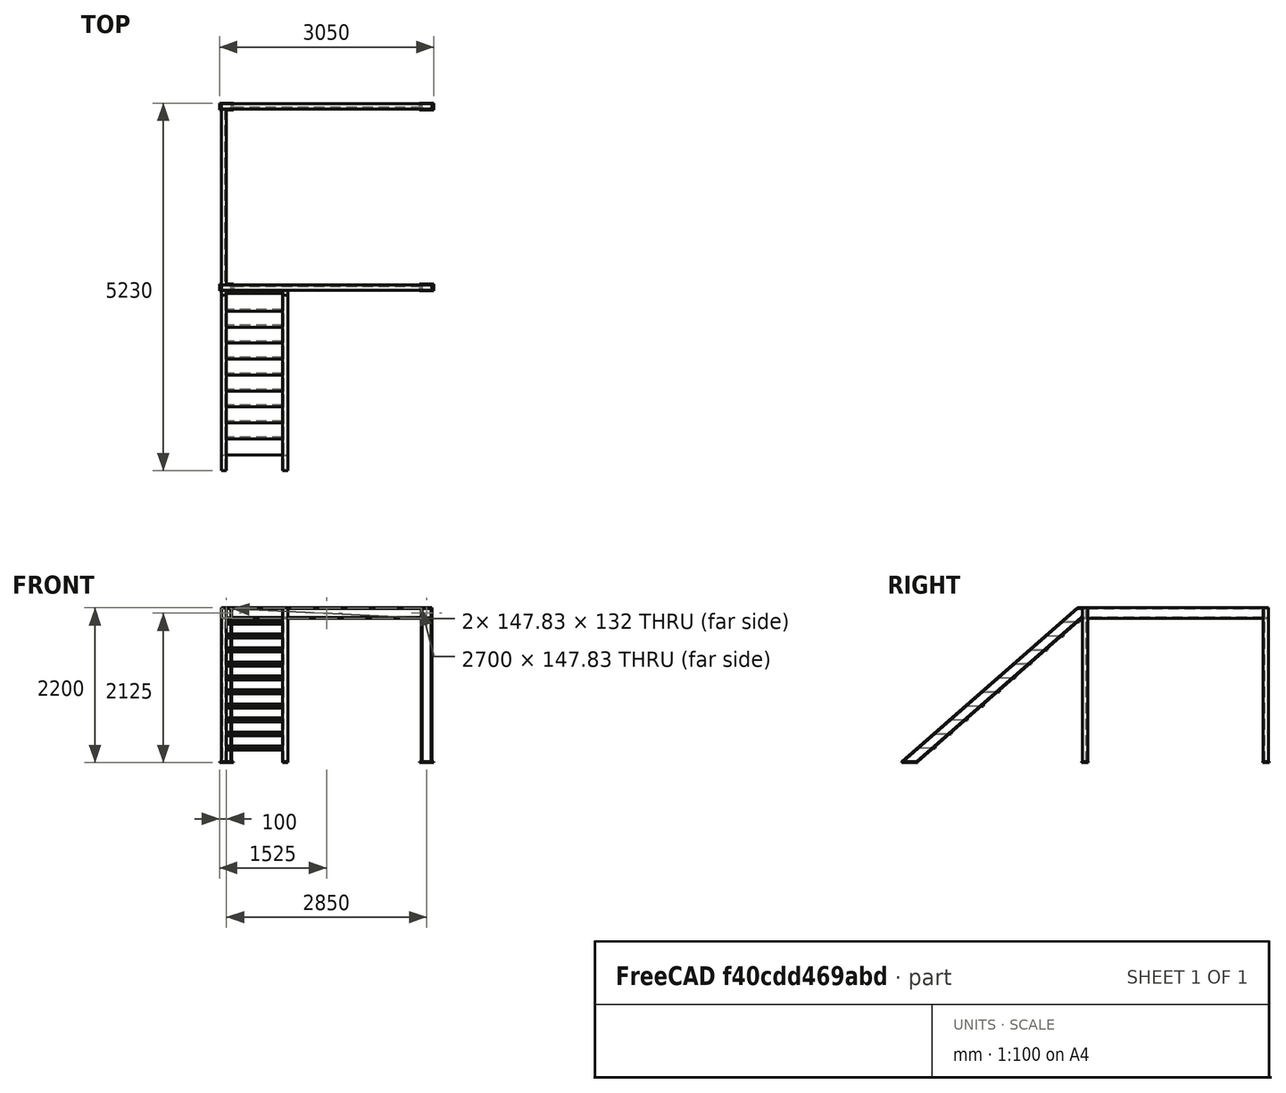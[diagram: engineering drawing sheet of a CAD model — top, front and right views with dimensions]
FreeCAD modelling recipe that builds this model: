
FCSTD DOCUMENT  (FreeCAD 0.21R30492 (Git))
Label: test2
License: All rights reserved
LicenseURL: http://en.wikipedia.org/wiki/All_rights_reserved
objects: App::FeaturePython×20, Part::FeaturePython×4, Part::Mirroring×2
note: 6 computed .brp shape members not serialized (recipe doc carries the construction recipe); baked Part::Feature solids carry a one-line shape summary decoded from their .brp

FEATURE [Part::FeaturePython] s06C150x75x9  # WARN: FeaturePython — macro-defined, semantics opaque (R4)
  B = 95
  BasePlate = true
  H = 2200
  L1 = 3000
  W = 200
  key = 5
  key1 = 1
  size = 3
  t0 = 6
FEATURE [Part::FeaturePython] C150x75x9  # WARN: FeaturePython — macro-defined, semantics opaque (R4)
  L = 2500
  Placement = pos=(2962.5,-2.62e-14,2125) rot=(1,0,0;1.5708rad)
  Solid = true
  size = 4
  standard = SS
FEATURE [Part::FeaturePython] s06C150x75x9_001  # a2plus imported part (geometry in sourceFile) (typed FeaturePython)
  a2p_Version = 0.4.60i
  fixedPosition = true
  localSourceObject = s06C150x75x9
  objectType = a2pPart
  sourceFile = converted
  subassemblyImport = false
  timeLastImport = 1.6781e+09
  updateColors = true
FEATURE [App::FeaturePython] pointIdentity_001  label="pointIdentity_001__s06C150x75x9_001"  # a2plus constraint (typed FeaturePython)
  Object1 = C150x75x9
  Object2 = s06C150x75x9_001
  ParentTreeObject = -> C150x75x9
  SubElement1 = Vertex23
  SubElement2 = Vertex22
  Suppressed = false
  Type = pointIdentity
FEATURE [App::FeaturePython] pointIdentity_001_mirror  label="pointIdentity_001__C150x75x9"  # a2plus constraint (typed FeaturePython)
  Object1 = C150x75x9
  Object2 = s06C150x75x9_001
  ParentTreeObject = -> s06C150x75x9_001
  SubElement1 = Vertex23
  SubElement2 = Vertex22
  Suppressed = false
  Type = pointIdentity
FEATURE [Part::Mirroring] mirror  label="C150x75x9 (mirrored) "
  Base = (1500,25.3073,2187.69)
  Normal = (1,0,0)
  Placement = pos=(2.88858e-06,1.12633e-05,-1.16466e-08) rot=(0,0,1;0rad)
  Source = -> C150x75x9
FEATURE [Part::Mirroring] mirror001  label="s06C150x75x9_001 (mirrored) "
  Base = (1538.3,-1250,1050)
  Normal = (0,-1,-1.19209e-07)
  Placement = pos=(0.000105519,0.000970233,-0.000317129) rot=(-0.994336,-0.022131,-0.103956;0rad)
  Source = -> s06C150x75x9_001
FEATURE [App::FeaturePython] planeCoincident_001  label="planeCoincident_001__stair"  # a2plus constraint (typed FeaturePython)
  Object1 = s06C150x75x9_001
  Object2 = stair
  SubElement1 = Face63
  SubElement2 = Face90
  Suppressed = false
  Type = plane
  directionConstraint = 1
  offset = 0
FEATURE [App::FeaturePython] planeCoincident_001_mirror  label="planeCoincident_001__s06C150x75x9_001"  # a2plus constraint (typed FeaturePython)
  Object1 = s06C150x75x9_001
  Object2 = stair
  SubElement1 = Face63
  SubElement2 = Face90
  Suppressed = false
  Type = plane
  directionConstraint = 1
  offset = 0
FEATURE [App::FeaturePython] planeCoincident_002  label="planeCoincident_002__s06C150x75x9_001 (mirrored) "  # a2plus constraint (typed FeaturePython)
  Object1 = s06C150x75x9_001
  Object2 = mirror001
  ParentTreeObject = -> s06C150x75x9_001
  SubElement1 = Face63
  SubElement2 = Face63
  Suppressed = false
  Type = plane
  directionConstraint = 0
  offset = 0
FEATURE [App::FeaturePython] planeCoincident_002_mirror  label="planeCoincident_002__s06C150x75x9_001"  # a2plus constraint (typed FeaturePython)
  Object1 = s06C150x75x9_001
  Object2 = mirror001
  ParentTreeObject = -> mirror001
  SubElement1 = Face63
  SubElement2 = Face63
  Suppressed = false
  Type = plane
  directionConstraint = 0
  offset = 0
FEATURE [App::FeaturePython] planeCoincident_003  label="planeCoincident_003__s06C150x75x9_001 (mirrored) "  # a2plus constraint (typed FeaturePython)
  Object1 = s06C150x75x9_001
  Object2 = mirror001
  ParentTreeObject = -> s06C150x75x9_001
  SubElement1 = Face63
  SubElement2 = Face63
  Suppressed = false
  Type = plane
  directionConstraint = 0
  offset = 0
FEATURE [App::FeaturePython] planeCoincident_003_mirror  label="planeCoincident_003__s06C150x75x9_001"  # a2plus constraint (typed FeaturePython)
  Object1 = s06C150x75x9_001
  Object2 = mirror001
  ParentTreeObject = -> mirror001
  SubElement1 = Face63
  SubElement2 = Face63
  Suppressed = false
  Type = plane
  directionConstraint = 0
  offset = 0
FEATURE [App::FeaturePython] axisCoincident_001  label="axisCoincident_001__s06C150x75x9_001 (mirrored) "  # a2plus constraint (typed FeaturePython)
  Object1 = mirror
  Object2 = mirror001
  ParentTreeObject = -> mirror
  SubElement1 = Edge36
  SubElement2 = Edge95
  Suppressed = false
  Type = axial
  directionConstraint = 0
  lockRotation = false
FEATURE [App::FeaturePython] axisCoincident_001_mirror  label="axisCoincident_001__C150x75x9 (mirrored) "  # a2plus constraint (typed FeaturePython)
  Object1 = mirror
  Object2 = mirror001
  ParentTreeObject = -> mirror001
  SubElement1 = Edge36
  SubElement2 = Edge95
  Suppressed = false
  Type = axial
  directionConstraint = 0
  lockRotation = false
FEATURE [App::FeaturePython] pointIdentity_003  label="pointIdentity_003__s06C150x75x9_001"  # a2plus constraint (typed FeaturePython)
  Object1 = mirror
  Object2 = s06C150x75x9_001
  ParentTreeObject = -> mirror
  SubElement1 = Vertex23
  SubElement2 = Vertex51
  Suppressed = false
  Type = pointIdentity
FEATURE [App::FeaturePython] pointIdentity_003_mirror  label="pointIdentity_003__C150x75x9 (mirrored) "  # a2plus constraint (typed FeaturePython)
  Object1 = mirror
  Object2 = s06C150x75x9_001
  ParentTreeObject = -> s06C150x75x9_001
  SubElement1 = Vertex23
  SubElement2 = Vertex51
  Suppressed = false
  Type = pointIdentity
FEATURE [App::FeaturePython] axisCoincident_002  label="axisCoincident_002__s06C150x75x9_001"  # a2plus constraint (typed FeaturePython)
  Object1 = mirror
  Object2 = s06C150x75x9_001
  ParentTreeObject = -> mirror
  SubElement1 = Edge35
  SubElement2 = Edge95
  Suppressed = false
  Type = axial
  directionConstraint = 0
  lockRotation = false
FEATURE [App::FeaturePython] axisCoincident_002_mirror  label="axisCoincident_002__C150x75x9 (mirrored) "  # a2plus constraint (typed FeaturePython)
  Object1 = mirror
  Object2 = s06C150x75x9_001
  ParentTreeObject = -> s06C150x75x9_001
  SubElement1 = Edge35
  SubElement2 = Edge95
  Suppressed = false
  Type = axial
  directionConstraint = 0
  lockRotation = false
FEATURE [App::FeaturePython] axisCoincident_003  label="axisCoincident_003__C150x75x9 (mirrored) "  # a2plus constraint (typed FeaturePython)
  Object1 = mirror001
  Object2 = mirror
  ParentTreeObject = -> mirror001
  SubElement1 = Edge69
  SubElement2 = Edge32
  Suppressed = false
  Type = axial
  directionConstraint = 1
  lockRotation = false
FEATURE [App::FeaturePython] axisCoincident_003_mirror  label="axisCoincident_003__s06C150x75x9_001 (mirrored) "  # a2plus constraint (typed FeaturePython)
  Object1 = mirror001
  Object2 = mirror
  ParentTreeObject = -> mirror
  SubElement1 = Edge69
  SubElement2 = Edge32
  Suppressed = false
  Type = axial
  directionConstraint = 1
  lockRotation = false
FEATURE [App::FeaturePython] planeCoincident_004  label="planeCoincident_004__s06C150x75x9_001 (mirrored) "  # a2plus constraint (typed FeaturePython)
  Object1 = s06C150x75x9_001
  Object2 = mirror001
  ParentTreeObject = -> s06C150x75x9_001
  SubElement1 = Face63
  SubElement2 = Face63
  Suppressed = false
  Type = plane
  directionConstraint = 0
  offset = 0
FEATURE [App::FeaturePython] planeCoincident_004_mirror  label="planeCoincident_004__s06C150x75x9_001"  # a2plus constraint (typed FeaturePython)
  Object1 = s06C150x75x9_001
  Object2 = mirror001
  ParentTreeObject = -> mirror001
  SubElement1 = Face63
  SubElement2 = Face63
  Suppressed = false
  Type = plane
  directionConstraint = 0
  offset = 0
FEATURE [App::FeaturePython] planeCoincident_005  label="planeCoincident_005__s06C150x75x9_001 (mirrored) "  # a2plus constraint (typed FeaturePython)
  Object1 = stair
  Object2 = mirror001
  SubElement1 = Face83
  SubElement2 = Face63
  Suppressed = false
  Type = plane
  directionConstraint = 0
  offset = 0
FEATURE [App::FeaturePython] planeCoincident_005_mirror  label="planeCoincident_005__stair"  # a2plus constraint (typed FeaturePython)
  Object1 = stair
  Object2 = mirror001
  SubElement1 = Face83
  SubElement2 = Face63
  Suppressed = false
  Type = plane
  directionConstraint = 0
  offset = 0
FEATURE [Part::FeaturePython] stair  # WARN: FeaturePython — macro-defined, semantics opaque (R4)
  B = 75
  Cy = 22.8
  H = 2200
  H0 = 150
  HighPlace = false
  L = 2500
  L1 = 70
  Placement = pos=(75,-5046.13,-103.808) rot=(0,0,1;1.5708rad)
  key = 0
  key1 = 0
  key2 = 2
  r1 = 10
  r2 = 5
  size = 1
  t = 9
  t1 = 6.5
  t2 = 10
  type = 0
  w = 800
